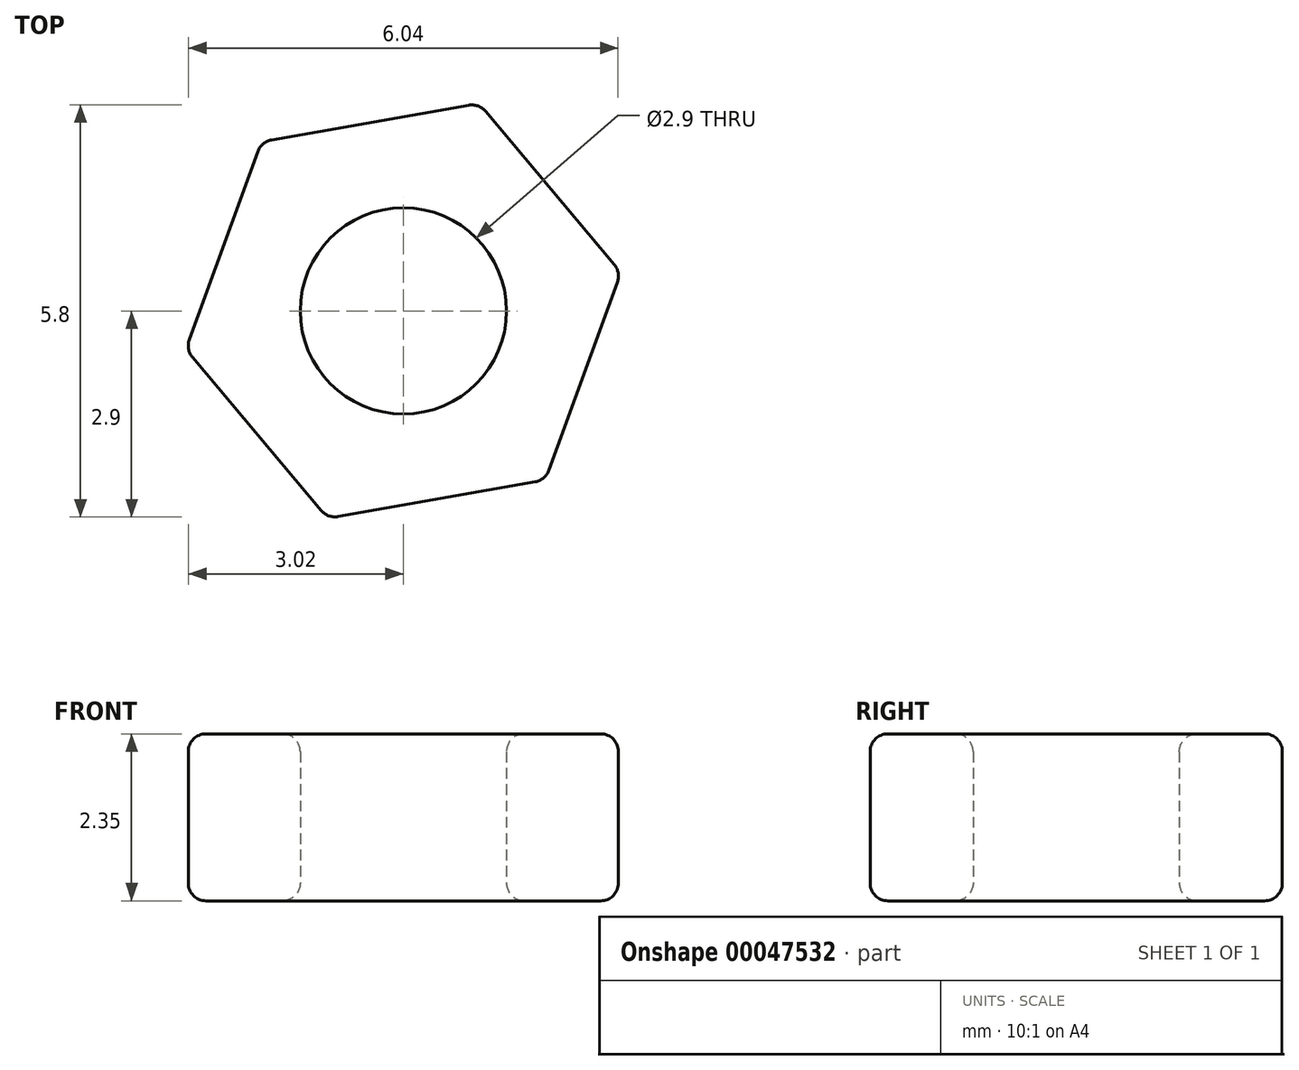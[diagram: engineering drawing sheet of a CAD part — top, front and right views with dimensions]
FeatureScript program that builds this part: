
annotation { "Feature Type Name" : "Feature", "Feature Type Description" : "" }
export const myFeature = defineFeature(function(context is Context, id is Id, definition is map)
    precondition{}
    {
        {
            var Q0;
            Q0=qCreatedBy(makeId("Top.planeOp"),FACE);
            var sketch = newSketch(context, id + "F0", { "sketchPlane" : qUnion([Q0])});
            skCircle(sketch, "E0.cCircle", {"center": v(0, 0) * mm, "radius": 3.1 * mm, "construction": true});
            skLineSegment(sketch, "E0.0", {"start": v(2, -2.38) * mm, "end": v(-1.06, -2.92) * mm});
            skLineSegment(sketch, "E0.1", {"start": v(-1.06, -2.92) * mm, "end": v(-3.06, -0.54) * mm});
            skLineSegment(sketch, "E0.2", {"start": v(-3.06, -0.54) * mm, "end": v(-2, 2.38) * mm});
            skLineSegment(sketch, "E0.3", {"start": v(-2, 2.38) * mm, "end": v(1.06, 2.92) * mm});
            skLineSegment(sketch, "E0.4", {"start": v(1.06, 2.92) * mm, "end": v(3.06, 0.54) * mm});
            skLineSegment(sketch, "E0.5", {"start": v(3.06, 0.54) * mm, "end": v(2, -2.38) * mm});
            skCircle(sketch, "E1", {"center": v(0, 0) * mm, "radius": 1.45 * mm});
            skSolve(sketch);
        }
        {
            var Q0;
            Q0 = qSketchRegion(id + "F0", true);
            extrude(context, id + "F1", {"entities" : qUnion([Q0]), "depth" : 2.35 * mm});
        }
        {
            var Q0;
            Q0=makeQuery(id+"F1.opExtrude","CAP_FACE",FACE,{"disambiguationData":[OSD([sQuery(id+"F0.wireOp",EDGE,"E0.0"),sQuery(id+"F0.wireOp",EDGE,"E0.1"),sQuery(id+"F0.wireOp",EDGE,"E0.2"),sQuery(id+"F0.wireOp",EDGE,"E0.3"),sQuery(id+"F0.wireOp",EDGE,"E0.4"),sQuery(id+"F0.wireOp",EDGE,"E0.5"),sQuery(id+"F0.wireOp",EDGE,"E1")])],"isStart":false});
            var Q1;
            Q1=makeQuery(id+"F1.opExtrude","CAP_FACE",FACE,{"disambiguationData":[OSD([sQuery(id+"F0.wireOp",EDGE,"E0.0"),sQuery(id+"F0.wireOp",EDGE,"E0.1"),sQuery(id+"F0.wireOp",EDGE,"E0.2"),sQuery(id+"F0.wireOp",EDGE,"E0.3"),sQuery(id+"F0.wireOp",EDGE,"E0.4"),sQuery(id+"F0.wireOp",EDGE,"E0.5"),sQuery(id+"F0.wireOp",EDGE,"E1")])],"isStart":true});
            var Q2;
            Q2=makeQuery(id+"F1.opExtrude","SWEPT_EDGE",EDGE,{"disambiguationData":[OSD([sQuery(id+"F0.wireOp",EDGE,"E0.2"),sQuery(id+"F0.wireOp",EDGE,"E0.3")])]});
            var Q3;
            Q3=makeQuery(id+"F1.opExtrude","SWEPT_EDGE",EDGE,{"disambiguationData":[OSD([sQuery(id+"F0.wireOp",EDGE,"E0.1"),sQuery(id+"F0.wireOp",EDGE,"E0.2")])]});
            var Q4;
            Q4=makeQuery(id+"F1.opExtrude","SWEPT_EDGE",EDGE,{"disambiguationData":[OSD([sQuery(id+"F0.wireOp",EDGE,"E0.0"),sQuery(id+"F0.wireOp",EDGE,"E0.1")])]});
            var Q5;
            Q5=makeQuery(id+"F1.opExtrude","SWEPT_EDGE",EDGE,{"disambiguationData":[OSD([sQuery(id+"F0.wireOp",EDGE,"E0.3"),sQuery(id+"F0.wireOp",EDGE,"E0.4")])]});
            var Q6;
            Q6=makeQuery(id+"F1.opExtrude","SWEPT_EDGE",EDGE,{"disambiguationData":[OSD([sQuery(id+"F0.wireOp",EDGE,"E0.4"),sQuery(id+"F0.wireOp",EDGE,"E0.5")])]});
            var Q7;
            Q7=makeQuery(id+"F1.opExtrude","SWEPT_EDGE",EDGE,{"disambiguationData":[OSD([sQuery(id+"F0.wireOp",EDGE,"E0.0"),sQuery(id+"F0.wireOp",EDGE,"E0.5")])]});
            fillet(context, id + "F2", {"entities" : qUnion([Q0, Q1, Q2, Q3, Q4, Q5, Q6, Q7]), "radius" : .25 * mm, "tangentPropagation" : true, "allowEdgeOverflow" : false});
        }
    });
